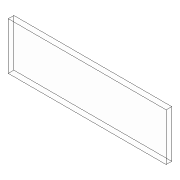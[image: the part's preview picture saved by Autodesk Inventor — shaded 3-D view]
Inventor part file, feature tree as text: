
AUTODESK INVENTOR PART (.ipt)
format: ipt  version: 2018.3 (Build 223284000, 284)  size: 72,192 bytes
history: native  units: in
note: dims shown in document units (in); Inventor stores cm internally (conversion verified against a paired STEP export)
features: extrude x1, sketch x1
ambient origin geometry x8: Origin, YZ Plane, XZ Plane, XY Plane, X Axis, Y Axis, Z Axis, Center Point
bodies: Solid1 (feature_tree)
feature tree (2):
  extrude  "Extrusion1"  Depth=0.675in
  sketch  "Sketch1"  dims[d0=2.25in d1=0.675in d2=0.08in d3=0.0in]
